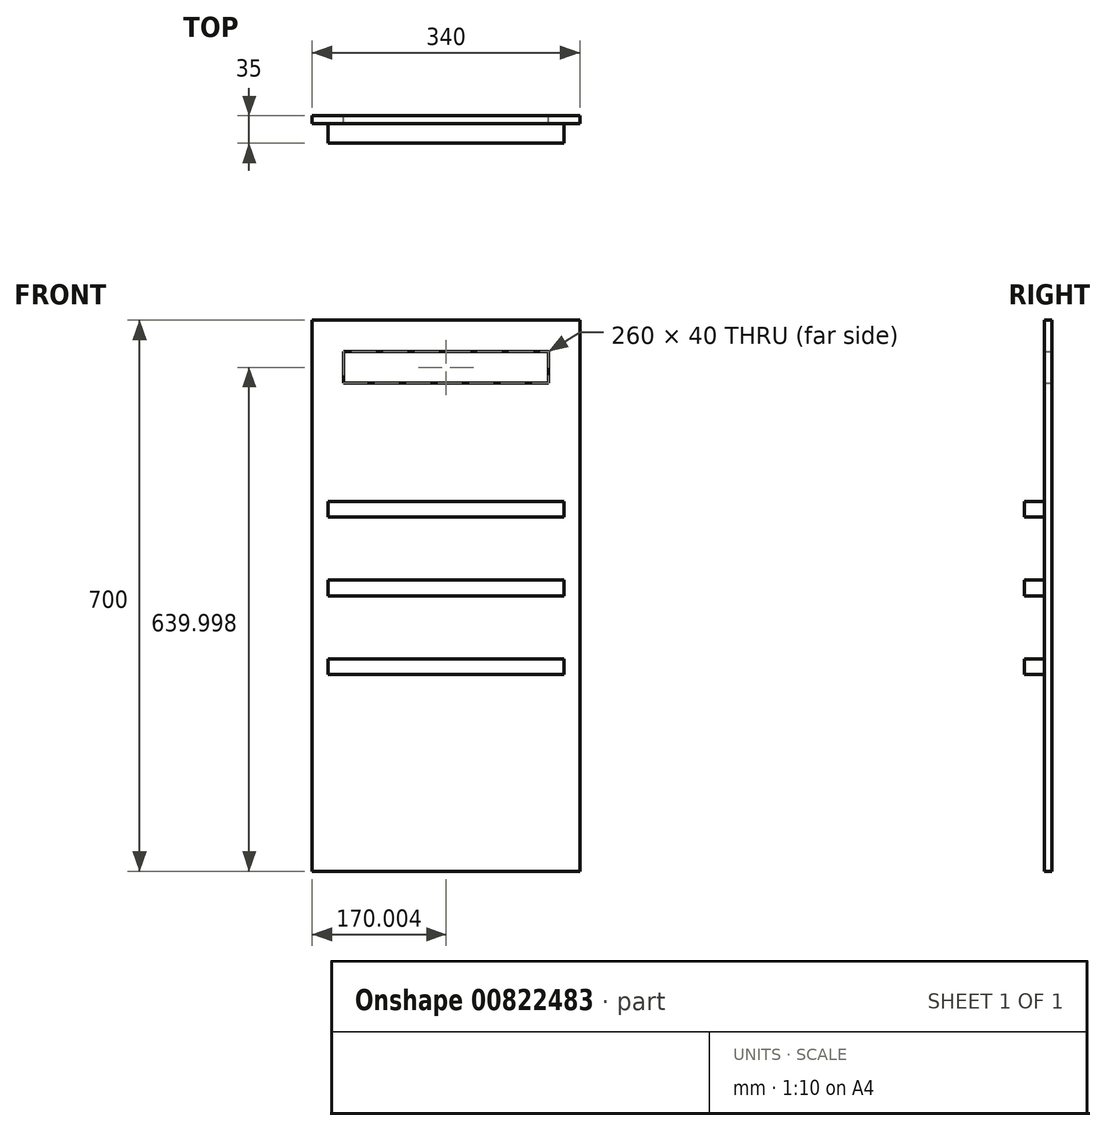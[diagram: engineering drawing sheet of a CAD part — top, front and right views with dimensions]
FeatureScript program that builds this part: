
annotation { "Feature Type Name" : "Feature", "Feature Type Description" : "" }
export const myFeature = defineFeature(function(context is Context, id is Id, definition is map)
    precondition{}
    {
        {
            var Q0;
            Q0=qCreatedBy(makeId("Front.planeOp"),FACE);
            var sketch = newSketch(context, id + "F0", { "sketchPlane" : qUnion([Q0])});
            skLineSegment(sketch, "E0.bottom", {"start": v(-322.95, 334.08) * mm, "end": v(17.05, 334.08) * mm});
            skLineSegment(sketch, "E0.top", {"start": v(-322.95, -365.92) * mm, "end": v(17.05, -365.92) * mm});
            skLineSegment(sketch, "E0.left", {"start": v(-322.95, 334.08) * mm, "end": v(-322.95, -365.92) * mm});
            skLineSegment(sketch, "E0.right", {"start": v(17.05, 334.08) * mm, "end": v(17.05, -365.92) * mm});
            skLineSegment(sketch, "E1.bottom", {"start": v(-282.95, 294.08) * mm, "end": v(-22.95, 294.08) * mm});
            skLineSegment(sketch, "E1.top", {"start": v(-282.95, 254.08) * mm, "end": v(-22.95, 254.08) * mm});
            skLineSegment(sketch, "E1.left", {"start": v(-282.95, 294.08) * mm, "end": v(-282.95, 254.08) * mm});
            skLineSegment(sketch, "E1.right", {"start": v(-22.95, 294.08) * mm, "end": v(-22.95, 254.08) * mm});
            skLineSegment(sketch, "E2.bottom", {"start": v(-302.95, 104.08) * mm, "end": v(-2.95, 104.08) * mm});
            skLineSegment(sketch, "E2.top", {"start": v(-302.95, 84.08) * mm, "end": v(-2.95, 84.08) * mm});
            skLineSegment(sketch, "E2.left", {"start": v(-302.95, 104.08) * mm, "end": v(-302.95, 84.08) * mm});
            skLineSegment(sketch, "E2.right", {"start": v(-2.95, 104.08) * mm, "end": v(-2.95, 84.08) * mm});
            skLineSegment(sketch, "E3.bottom", {"start": v(-302.95, 4.08) * mm, "end": v(-2.95, 4.08) * mm});
            skLineSegment(sketch, "E3.top", {"start": v(-302.95, -15.92) * mm, "end": v(-2.95, -15.92) * mm});
            skLineSegment(sketch, "E3.left", {"start": v(-302.95, 4.08) * mm, "end": v(-302.95, -15.92) * mm});
            skLineSegment(sketch, "E3.right", {"start": v(-2.95, 4.08) * mm, "end": v(-2.95, -15.92) * mm});
            skLineSegment(sketch, "E4.bottom", {"start": v(-302.95, -95.92) * mm, "end": v(-2.95, -95.92) * mm});
            skLineSegment(sketch, "E4.top", {"start": v(-302.95, -115.92) * mm, "end": v(-2.95, -115.92) * mm});
            skLineSegment(sketch, "E4.left", {"start": v(-302.95, -95.92) * mm, "end": v(-302.95, -115.92) * mm});
            skLineSegment(sketch, "E4.right", {"start": v(-2.95, -95.92) * mm, "end": v(-2.95, -115.92) * mm});
            skSolve(sketch);
        }
        {
            var Q0;
            Q0=makeQuery(id+"F0.imprint","IMPRINT",FACE,{"disambiguationData":[TD([[makeQuery(id+"F0.imprint","IMPRINT",EDGE,{"derivedFrom":sQuery(id+"F0.wireOp",EDGE,"E0.bottom")}),-1.0]])]});
            extrude(context, id + "F1", {"entities" : qUnion([Q0]), "depth" : 10 * mm, "offsetDistance" : 25.4 * mm});
        }
        {
            var Q0;
            Q0=makeQuery(id+"F0.imprint","IMPRINT",FACE,{"disambiguationData":[TD([[makeQuery(id+"F0.imprint","IMPRINT",EDGE,{"derivedFrom":sQuery(id+"F0.wireOp",EDGE,"E2.bottom")}),-1.0]])]});
            var Q1;
            Q1=makeQuery(id+"F0.imprint","IMPRINT",FACE,{"disambiguationData":[TD([[makeQuery(id+"F0.imprint","IMPRINT",EDGE,{"derivedFrom":sQuery(id+"F0.wireOp",EDGE,"E3.bottom")}),-1.0]])]});
            var Q2;
            Q2=makeQuery(id+"F0.imprint","IMPRINT",FACE,{"disambiguationData":[TD([[makeQuery(id+"F0.imprint","IMPRINT",EDGE,{"derivedFrom":sQuery(id+"F0.wireOp",EDGE,"E4.bottom")}),-1.0]])]});
            extrude(context, id + "F2", {"entities" : qUnion([Q0, Q1, Q2]), "operationType" : NewBodyOperationType.ADD, "depth" : 35 * mm, "offsetDistance" : 25 * mm});
        }
    });
